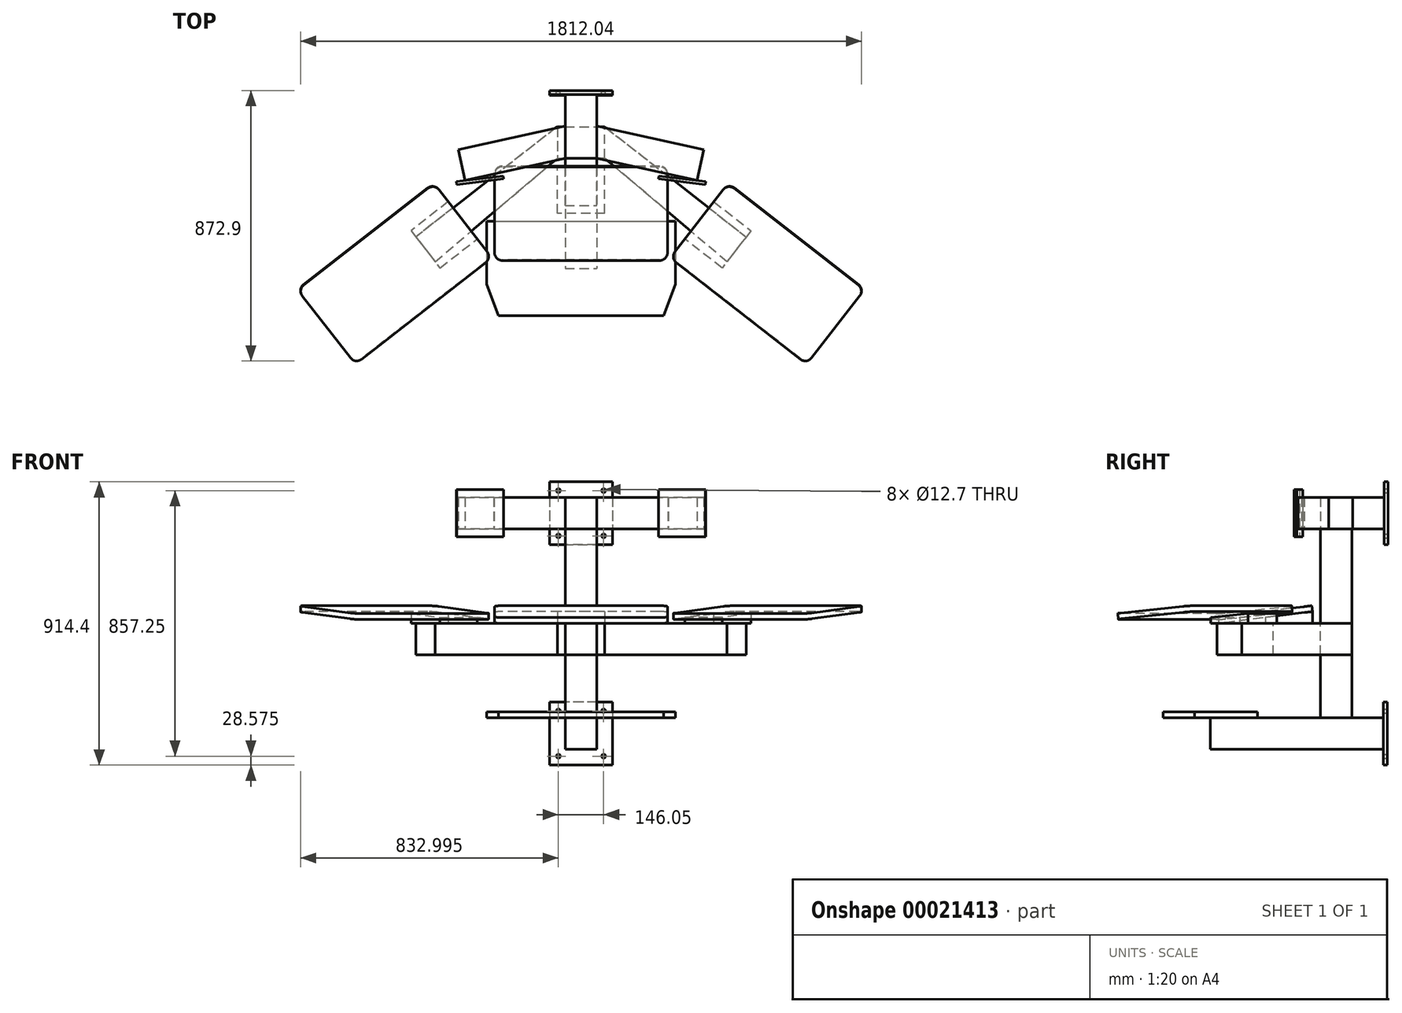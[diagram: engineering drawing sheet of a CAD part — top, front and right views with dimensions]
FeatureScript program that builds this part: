
annotation { "Feature Type Name" : "Feature", "Feature Type Description" : "" }
export const myFeature = defineFeature(function(context is Context, id is Id, definition is map)
    precondition{}
    {
        {
            var Q0;
            Q0=qCreatedBy(makeId("Top.planeOp"),FACE);
            var sketch = newSketch(context, id + "F0", { "sketchPlane" : qUnion([Q0])});
            skLineSegment(sketch, "E0", {"start": v(0, 189.9) * mm, "end": v(-50.8, 189.9) * mm});
            skLineSegment(sketch, "E1", {"start": v(-50.8, 189.9) * mm, "end": v(-50.8, 88.3) * mm});
            skLineSegment(sketch, "E2", {"start": v(-50.8, 88.3) * mm, "end": v(-396.31, 11.25) * mm});
            skLineSegment(sketch, "E3", {"start": v(-396.31, 11.25) * mm, "end": v(-374.2, -87.91) * mm});
            skLineSegment(sketch, "E4", {"start": v(-374.2, -87.91) * mm, "end": v(-50.8, -15.8) * mm});
            skLineSegment(sketch, "E5", {"start": v(-50.8, -15.8) * mm, "end": v(0, -15.8) * mm});
            skLineSegment(sketch, "E6", {"start": v(0, -15.8) * mm, "end": v(0, 189.9) * mm});
            skLineSegment(sketch, "E7.MirrorCS", {"start": v(0, 189.9) * mm, "end": v(50.8, 189.9) * mm});
            skLineSegment(sketch, "E8.MirrorCS", {"start": v(50.8, 189.9) * mm, "end": v(50.8, 88.3) * mm});
            skLineSegment(sketch, "E9.MirrorCS", {"start": v(50.8, 88.3) * mm, "end": v(396.31, 11.25) * mm});
            skLineSegment(sketch, "E10.MirrorCS", {"start": v(396.31, 11.25) * mm, "end": v(374.2, -87.91) * mm});
            skLineSegment(sketch, "E11.MirrorCS", {"start": v(374.2, -87.91) * mm, "end": v(50.8, -15.8) * mm});
            skLineSegment(sketch, "E12.MirrorCS", {"start": v(50.8, -15.8) * mm, "end": v(0, -15.8) * mm});
            skLineSegment(sketch, "E13", {"start": v(-50.8, 88.3) * mm, "end": v(-50.8, -15.8) * mm});
            skLineSegment(sketch, "E14", {"start": v(50.8, 88.3) * mm, "end": v(50.8, -15.8) * mm});
            skLineSegment(sketch, "E15", {"start": v(-50.8, 189.9) * mm, "end": v(-101.6, 189.9) * mm});
            skLineSegment(sketch, "E16", {"start": v(-101.6, 189.9) * mm, "end": v(-101.6, 202.6) * mm});
            skLineSegment(sketch, "E17", {"start": v(-101.6, 202.6) * mm, "end": v(0, 202.6) * mm});
            skLineSegment(sketch, "E18", {"start": v(0, 202.6) * mm, "end": v(0, 189.9) * mm});
            skLineSegment(sketch, "E19.MirrorCS", {"start": v(101.6, 202.6) * mm, "end": v(0, 202.6) * mm});
            skLineSegment(sketch, "E20.MirrorCS", {"start": v(101.6, 189.9) * mm, "end": v(101.6, 202.6) * mm});
            skLineSegment(sketch, "E21.MirrorCS", {"start": v(50.8, 189.9) * mm, "end": v(101.6, 189.9) * mm});
            skLineSegment(sketch, "E22", {"start": v(-374.2, -87.91) * mm, "end": v(-280.2, -76.7) * mm});
            skLineSegment(sketch, "E23", {"start": v(-280.2, -76.7) * mm, "end": v(-282.27, -67.41) * mm});
            skLineSegment(sketch, "E24", {"start": v(-280.2, -76.7) * mm, "end": v(-251.54, -73.3) * mm});
            skLineSegment(sketch, "E25", {"start": v(-251.54, -73.3) * mm, "end": v(-250.4, -82.75) * mm});
            skLineSegment(sketch, "E26", {"start": v(-250.4, -82.75) * mm, "end": v(-401.74, -100.78) * mm});
            skLineSegment(sketch, "E27", {"start": v(-401.74, -100.78) * mm, "end": v(-402.86, -91.33) * mm});
            skLineSegment(sketch, "E28", {"start": v(-402.86, -91.33) * mm, "end": v(-374.2, -87.91) * mm});
            skLineSegment(sketch, "E29.MirrorCS", {"start": v(280.2, -76.7) * mm, "end": v(282.27, -67.41) * mm});
            skLineSegment(sketch, "E30.MirrorCS", {"start": v(251.54, -73.3) * mm, "end": v(250.4, -82.75) * mm});
            skLineSegment(sketch, "E31.MirrorCS", {"start": v(280.2, -76.7) * mm, "end": v(251.54, -73.3) * mm});
            skLineSegment(sketch, "E32.MirrorCS", {"start": v(374.2, -87.91) * mm, "end": v(280.2, -76.7) * mm});
            skLineSegment(sketch, "E33.MirrorCS", {"start": v(402.86, -91.33) * mm, "end": v(374.2, -87.91) * mm});
            skLineSegment(sketch, "E34.MirrorCS", {"start": v(401.74, -100.78) * mm, "end": v(402.86, -91.33) * mm});
            skLineSegment(sketch, "E35.MirrorCS", {"start": v(250.4, -82.75) * mm, "end": v(401.74, -100.78) * mm});
            skLineSegment(sketch, "E36", {"start": v(50.8, 88.3) * mm, "end": v(-50.8, 88.3) * mm});
            skPoint(sketch, "E37", {"position": v(0, 88.3) * mm});
            skPoint(sketch, "E38", {"position": v(-326.07, -91.77) * mm});
            skPoint(sketch, "E39", {"position": v(326.07, -91.77) * mm});
            skSolve(sketch);
        }
        {
            var Q0;
            Q0=makeQuery(id+"F0.imprint","IMPRINT",FACE,{"disambiguationData":[TD([[makeQuery(id+"F0.imprint","IMPRINT",EDGE,{"derivedFrom":sQuery(id+"F0.wireOp",EDGE,"E0")}),1.0]])]});
            var Q1;
            Q1=makeQuery(id+"F0.imprint","IMPRINT",FACE,{"disambiguationData":[TD([[makeQuery(id+"F0.imprint","IMPRINT",EDGE,{"derivedFrom":sQuery(id+"F0.wireOp",EDGE,"E6")}),-1.0]])]});
            var Q2;
            {var subQ4=sQuery(id+"F0.wireOp",EDGE,"E5");Q2=makeQuery(id+"F0.imprint","IMPRINT",FACE,{"disambiguationData":[TD([[makeQuery(id+"F0.imprint","IMPRINT",EDGE,{"derivedFrom":subQ4}),1.0]])]});}
            extrude(context, id + "F1", {"entities" : qUnion([Q0, Q1, Q2]), "depth" : 101.6 * mm, "symmetric" : true});
        }
        {
            var Q0;
            Q0=makeQuery(id+"F0.imprint","IMPRINT",FACE,{"disambiguationData":[TD([[makeQuery(id+"F0.imprint","IMPRINT",EDGE,{"derivedFrom":sQuery(id+"F0.wireOp",EDGE,"E0")}),-1.0]])]});
            var Q1;
            Q1=makeQuery(id+"F0.imprint","IMPRINT",FACE,{"disambiguationData":[TD([[makeQuery(id+"F0.imprint","IMPRINT",EDGE,{"derivedFrom":sQuery(id+"F0.wireOp",EDGE,"E18")}),1.0]])]});
            extrude(context, id + "F2", {"entities" : qUnion([Q0, Q1]), "depth" : 203.2 * mm, "symmetric" : true});
        }
        {
            var Q0;
            Q0=makeQuery(id+"F0.imprint","IMPRINT",FACE,{"disambiguationData":[TD([[makeQuery(id+"F0.imprint","IMPRINT",EDGE,{"derivedFrom":sQuery(id+"F0.wireOp",EDGE,"E2")}),1.0]])]});
            extrude(context, id + "F3", {"entities" : qUnion([Q0]), "depth" : 101.6 * mm, "symmetric" : true});
        }
        {
            var Q0;
            Q0=makeQuery(id+"F0.imprint","IMPRINT",FACE,{"disambiguationData":[TD([[makeQuery(id+"F0.imprint","IMPRINT",EDGE,{"derivedFrom":sQuery(id+"F0.wireOp",EDGE,"E9.MirrorCS")}),-1.0]])]});
            extrude(context, id + "F4", {"entities" : qUnion([Q0]), "depth" : 101.6 * mm, "symmetric" : true});
        }
        {
            var Q0;
            {var subQ1=sQuery(id+"F0.wireOp",EDGE,"E22");Q0=makeQuery(id+"F0.imprint","IMPRINT",FACE,{"disambiguationData":[TD([[makeQuery(id+"F0.imprint","IMPRINT",EDGE,{"derivedFrom":subQ1}),1.0]])]});}
            extrude(context, id + "F5", {"entities" : qUnion([Q0]), "depth" : 101.6 * mm, "symmetric" : true});
        }
        {
            var Q0;
            {var subQ0=sQuery(id+"F0.wireOp",EDGE,"E29.MirrorCS");Q0=makeQuery(id+"F0.imprint","IMPRINT",FACE,{"disambiguationData":[TD([[makeQuery(id+"F0.imprint","IMPRINT",EDGE,{"derivedFrom":subQ0}),-1.0]])]});}
            extrude(context, id + "F6", {"entities" : qUnion([Q0]), "depth" : 101.6 * mm, "symmetric" : true});
        }
        {
            var Q0;
            Q0=makeQuery(id+"F0.imprint","IMPRINT",FACE,{"disambiguationData":[TD([[makeQuery(id+"F0.imprint","IMPRINT",EDGE,{"derivedFrom":sQuery(id+"F0.wireOp",EDGE,"E22")}),-1.0]])]});
            var Q1;
            Q1=makeQuery(id+"F0.imprint","IMPRINT",FACE,{"disambiguationData":[TD([[makeQuery(id+"F0.imprint","IMPRINT",EDGE,{"derivedFrom":sQuery(id+"F0.wireOp",EDGE,"E30.MirrorCS")}),1.0]])]});
            extrude(context, id + "F7", {"entities" : qUnion([Q0, Q1]), "depth" : 152.4 * mm, "symmetric" : true});
        }
        {
            var Q0;
            Q0=makeQuery(id+"F2.opExtrude","SWEPT_FACE",FACE,{"disambiguationData":[OSD([sQuery(id+"F0.wireOp",EDGE,"E0"),sQuery(id+"F0.wireOp",EDGE,"E15"),sQuery(id+"F0.wireOp",EDGE,"E21.MirrorCS"),sQuery(id+"F0.wireOp",EDGE,"E7.MirrorCS")])]});
            var sketch = newSketch(context, id + "F8", { "sketchPlane" : qUnion([Q0])});
            skLineSegment(sketch, "E40", {"start": v(-73.02, 101.6) * mm, "end": v(-73.02, -101.6) * mm, "construction": true});
            skLineSegment(sketch, "E41", {"start": v(73.03, -101.6) * mm, "end": v(73.03, 101.6) * mm, "construction": true});
            skLineSegment(sketch, "E42", {"start": v(101.6, 73.02) * mm, "end": v(-101.6, 73.02) * mm, "construction": true});
            skLineSegment(sketch, "E43", {"start": v(-101.6, -73.03) * mm, "end": v(101.6, -73.03) * mm, "construction": true});
            skPoint(sketch, "E44", {"position": v(-73.02, 73.02) * mm});
            skPoint(sketch, "E45", {"position": v(73.03, 73.02) * mm});
            skPoint(sketch, "E46", {"position": v(73.03, -73.03) * mm});
            skPoint(sketch, "E47", {"position": v(-73.02, -73.03) * mm});
            skSolve(sketch);
        }
        {
            var Q0;
            Q0=makeQuery(id+"F1.opExtrude","CAP_FACE",FACE,{"disambiguationData":[OSD([sQuery(id+"F0.wireOp",EDGE,"E0"),sQuery(id+"F0.wireOp",EDGE,"E1"),sQuery(id+"F0.wireOp",EDGE,"E5"),sQuery(id+"F0.wireOp",EDGE,"E8.MirrorCS"),sQuery(id+"F0.wireOp",EDGE,"E12.MirrorCS"),sQuery(id+"F0.wireOp",EDGE,"E13"),sQuery(id+"F0.wireOp",EDGE,"E14"),sQuery(id+"F0.wireOp",EDGE,"E7.MirrorCS")])],"isStart":true});
            var sketch = newSketch(context, id + "F9", { "sketchPlane" : qUnion([Q0])});
            skLineSegment(sketch, "E48.bottom", {"start": v(-50.8, 15.8) * mm, "end": v(50.8, 15.8) * mm});
            skLineSegment(sketch, "E48.top", {"start": v(-50.8, -85.8) * mm, "end": v(50.8, -85.8) * mm});
            skLineSegment(sketch, "E48.left", {"start": v(-50.8, 15.8) * mm, "end": v(-50.8, -85.8) * mm});
            skLineSegment(sketch, "E48.right", {"start": v(50.8, 15.8) * mm, "end": v(50.8, -85.8) * mm});
            skSolve(sketch);
        }
        {
            var Q0;
            Q0=makeQuery(id+"F9.imprint","IMPRINT",FACE,{"disambiguationData":[TD([[makeQuery(id+"F9.imprint","IMPRINT",EDGE,{"derivedFrom":sQuery(id+"F9.wireOp",EDGE,"E48.bottom")}),1.0]])]});
            extrude(context, id + "F10", {"entities" : qUnion([Q0]), "depth" : 609.6 * mm});
        }
        {
            var Q0;
            Q0=makeQuery(id+"F10.opExtrude","CAP_FACE",FACE,{"disambiguationData":[OSD([sQuery(id+"F9.wireOp",EDGE,"E48.bottom"),sQuery(id+"F9.wireOp",EDGE,"E48.top"),sQuery(id+"F9.wireOp",EDGE,"E48.left"),sQuery(id+"F9.wireOp",EDGE,"E48.right")])],"isStart":false});
            var sketch = newSketch(context, id + "F11", { "sketchPlane" : qUnion([Q0])});
            skLineSegment(sketch, "E49", {"start": v(-50.8, 15.8) * mm, "end": v(-50.8, 371.4) * mm});
            skLineSegment(sketch, "E50", {"start": v(-50.8, 371.4) * mm, "end": v(0, 371.4) * mm});
            skLineSegment(sketch, "E51", {"start": v(0, 371.4) * mm, "end": v(0, -187.4) * mm});
            skLineSegment(sketch, "E52", {"start": v(0, -187.4) * mm, "end": v(-50.8, -187.4) * mm});
            skLineSegment(sketch, "E53", {"start": v(-50.8, -187.4) * mm, "end": v(-50.8, 15.8) * mm});
            skLineSegment(sketch, "E54.MirrorCS", {"start": v(50.8, 371.4) * mm, "end": v(0, 371.4) * mm});
            skLineSegment(sketch, "E55.MirrorCS", {"start": v(50.8, 15.8) * mm, "end": v(50.8, 371.4) * mm});
            skLineSegment(sketch, "E56.MirrorCS", {"start": v(50.8, -187.4) * mm, "end": v(50.8, 15.8) * mm});
            skLineSegment(sketch, "E57.MirrorCS", {"start": v(0, -187.4) * mm, "end": v(50.8, -187.4) * mm});
            skLineSegment(sketch, "E58.MirrorCS", {"start": v(-50.8, 15.8) * mm, "end": v(50.8, 15.8) * mm});
            skLineSegment(sketch, "E59", {"start": v(0, -209.13) * mm, "end": v(0, -187.4) * mm});
            skSolve(sketch);
        }
        {
            var Q0;
            {var subQ3=sQuery(id+"F11.wireOp",EDGE,"E49");Q0=makeQuery(id+"F11.imprint","IMPRINT",FACE,{"disambiguationData":[TD([[makeQuery(id+"F11.imprint","IMPRINT",EDGE,{"derivedFrom":subQ3}),-1.0]])]});}
            var Q1;
            {var subQ4=sQuery(id+"F11.wireOp",EDGE,"E54.MirrorCS");Q1=makeQuery(id+"F11.imprint","IMPRINT",FACE,{"disambiguationData":[TD([[makeQuery(id+"F11.imprint","IMPRINT",EDGE,{"derivedFrom":subQ4}),1.0]])]});}
            var Q2;
            {var subQ1=sQuery(id+"F11.wireOp",EDGE,"E51");var subQ5=sQuery(id+"F11.wireOp",EDGE,"E58.MirrorCS");var subQ6=makeQuery(id+"F11.imprint","INTERSECT",VERTEX,{"derivedFrom":[subQ1,subQ5]});Q2=makeQuery(id+"F11.imprint","IMPRINT",FACE,{"disambiguationData":[TD([[makeQuery(id+"F11.imprint","IMPRINT",EDGE,{"disambiguationData":[TD([[subQ6,-1.0]])],"derivedFrom":subQ1}),1.0]])]});}
            var Q3;
            {var subQ1=sQuery(id+"F11.wireOp",EDGE,"E51");var subQ5=sQuery(id+"F11.wireOp",EDGE,"E58.MirrorCS");var subQ6=makeQuery(id+"F11.imprint","INTERSECT",VERTEX,{"derivedFrom":[subQ1,subQ5]});Q3=makeQuery(id+"F11.imprint","IMPRINT",FACE,{"disambiguationData":[TD([[makeQuery(id+"F11.imprint","IMPRINT",EDGE,{"disambiguationData":[TD([[subQ6,-1.0]])],"derivedFrom":subQ1}),-1.0]])]});}
            var Q4;
            {var subQ5=sQuery(id+"F11.wireOp",EDGE,"E52");Q4=makeQuery(id+"F11.imprint","IMPRINT",FACE,{"disambiguationData":[TD([[makeQuery(id+"F11.imprint","IMPRINT",EDGE,{"derivedFrom":subQ5}),-1.0]])]});}
            var Q5;
            {var subQ5=sQuery(id+"F11.wireOp",EDGE,"E57.MirrorCS");Q5=makeQuery(id+"F11.imprint","IMPRINT",FACE,{"disambiguationData":[TD([[makeQuery(id+"F11.imprint","IMPRINT",EDGE,{"derivedFrom":subQ5}),1.0]])]});}
            extrude(context, id + "F12", {"entities" : qUnion([Q0, Q1, Q2, Q3, Q4, Q5]), "depth" : 101.6 * mm});
        }
        {
            var Q0;
            Q0=makeQuery(id+"F12.opExtrude","SWEPT_FACE",FACE,{"disambiguationData":[OSD([sQuery(id+"F11.wireOp",EDGE,"E57.MirrorCS"),sQuery(id+"F11.wireOp",EDGE,"E52")])]});
            var sketch = newSketch(context, id + "F13", { "sketchPlane" : qUnion([Q0])});
            skLineSegment(sketch, "E60.rect.bottom", {"start": v(-101.6, -609.6) * mm, "end": v(101.6, -609.6) * mm});
            skLineSegment(sketch, "E60.rect.top", {"start": v(-101.6, -812.8) * mm, "end": v(101.6, -812.8) * mm});
            skLineSegment(sketch, "E60.rect.left", {"start": v(-101.6, -609.6) * mm, "end": v(-101.6, -812.8) * mm});
            skLineSegment(sketch, "E60.rect.right", {"start": v(101.6, -609.6) * mm, "end": v(101.6, -812.8) * mm});
            skPoint(sketch, "E60.rect.middle", {"position": v(0, -711.2) * mm});
            skLineSegment(sketch, "E61", {"start": v(-50.8, -711.2) * mm, "end": v(50.8, -711.2) * mm, "construction": true});
            skLineSegment(sketch, "E62", {"start": v(0, -660.4) * mm, "end": v(0, -762) * mm, "construction": true});
            skLineSegment(sketch, "E63", {"start": v(-101.6, -638.18) * mm, "end": v(101.6, -638.18) * mm, "construction": true});
            skLineSegment(sketch, "E64", {"start": v(101.6, -784.23) * mm, "end": v(-101.6, -784.23) * mm, "construction": true});
            skLineSegment(sketch, "E65", {"start": v(-73.03, -609.6) * mm, "end": v(-73.03, -812.8) * mm, "construction": true});
            skLineSegment(sketch, "E66", {"start": v(73.02, -812.8) * mm, "end": v(73.02, -609.6) * mm, "construction": true});
            skPoint(sketch, "E67", {"position": v(-73.03, -638.18) * mm});
            skPoint(sketch, "E68", {"position": v(73.02, -638.18) * mm});
            skPoint(sketch, "E69", {"position": v(73.02, -784.23) * mm});
            skPoint(sketch, "E70", {"position": v(-73.03, -784.23) * mm});
            skSolve(sketch);
        }
        {
            var Q0;
            Q0=makeQuery(id+"F13.imprint","IMPRINT",FACE,{"disambiguationData":[TD([[makeQuery(id+"F13.imprint","IMPRINT",EDGE,{"derivedFrom":sQuery(id+"F13.wireOp",EDGE,"E60.rect.bottom")}),-1.0]])]});
            var Q1;
            {var subQ1=sQuery(id+"F11.wireOp",EDGE,"E52");Q1=makeQuery(id+"F13.imprint","IMPRINT",FACE,{"disambiguationData":[TD([[makeQuery(id+"F13.imprint","IMPRINT",EDGE,{"derivedFrom":makeQuery(id+"F12.opExtrude","SWEPT_EDGE",EDGE,{"disambiguationData":[OSD([sQuery(id+"F11.wireOp",EDGE,"E53"),subQ1])]})}),1.0]])]});}
            extrude(context, id + "F14", {"entities" : qUnion([Q0, Q1]), "depth" : 12.7 * mm});
        }
        {
            var Q0;
            Q0=sQuery(id+"F8.wireOp",VERTEX,"E44");
            var Q1;
            Q1=sQuery(id+"F8.wireOp",VERTEX,"E45");
            var Q2;
            Q2=sQuery(id+"F8.wireOp",VERTEX,"E46");
            var Q3;
            Q3=sQuery(id+"F8.wireOp",VERTEX,"E47");
            var Q4;
            Q4=sQuery(id+"F13.wireOp",VERTEX,"E67");
            var Q5;
            Q5=sQuery(id+"F13.wireOp",VERTEX,"E68");
            var Q6;
            Q6=sQuery(id+"F13.wireOp",VERTEX,"E69");
            var Q7;
            Q7=sQuery(id+"F13.wireOp",VERTEX,"E70");
            var Q8;
            Q8=makeQuery(id+"F2.opExtrude","SWEPT_BODY",BODY,{"disambiguationData":[OSD([sQuery(id+"F0.wireOp",EDGE,"E0"),sQuery(id+"F0.wireOp",EDGE,"E15"),sQuery(id+"F0.wireOp",EDGE,"E16"),sQuery(id+"F0.wireOp",EDGE,"E17"),sQuery(id+"F0.wireOp",EDGE,"E19.MirrorCS"),sQuery(id+"F0.wireOp",EDGE,"E20.MirrorCS"),sQuery(id+"F0.wireOp",EDGE,"E21.MirrorCS"),sQuery(id+"F0.wireOp",EDGE,"E7.MirrorCS")])]});
            hole(context, id + "F15", {"style" : HoleStyle.SIMPLE, "holeDiameter" : 12.7 * mm, "endStyle" : HoleEndStyle.THROUGH, "locations" : qUnion([Q0, Q1, Q2, Q3, Q4, Q5, Q6, Q7]), "scope" : qUnion([Q8])});
        }
        {
            var Q0;
            Q0=sQuery(id+"F13.wireOp",VERTEX,"E67");
            var Q1;
            Q1=sQuery(id+"F13.wireOp",VERTEX,"E68");
            var Q2;
            Q2=sQuery(id+"F13.wireOp",VERTEX,"E69");
            var Q3;
            Q3=sQuery(id+"F13.wireOp",VERTEX,"E70");
            var Q4;
            Q4=makeQuery(id+"F14.opExtrude","SWEPT_BODY",BODY,{"disambiguationData":[OSD([sQuery(id+"F13.wireOp",EDGE,"E60.rect.bottom"),sQuery(id+"F13.wireOp",EDGE,"E60.rect.top"),sQuery(id+"F13.wireOp",EDGE,"E60.rect.left"),sQuery(id+"F13.wireOp",EDGE,"E60.rect.right")])]});
            hole(context, id + "F16", {"style" : HoleStyle.SIMPLE, "holeDiameter" : 12.7 * mm, "endStyle" : HoleEndStyle.THROUGH, "oppositeDirection" : true, "locations" : qUnion([Q0, Q1, Q2, Q3]), "scope" : qUnion([Q4])});
        }
        {
            var Q0;
            Q0=makeQuery(id+"F12.opExtrude","CAP_FACE",FACE,{"disambiguationData":[OSD([sQuery(id+"F11.wireOp",EDGE,"E49"),sQuery(id+"F11.wireOp",EDGE,"E50"),sQuery(id+"F11.wireOp",EDGE,"E53"),sQuery(id+"F11.wireOp",EDGE,"E54.MirrorCS"),sQuery(id+"F11.wireOp",EDGE,"E55.MirrorCS"),sQuery(id+"F11.wireOp",EDGE,"E56.MirrorCS"),sQuery(id+"F11.wireOp",EDGE,"E57.MirrorCS"),sQuery(id+"F11.wireOp",EDGE,"E52")])],"isStart":true});
            var sketch = newSketch(context, id + "F17", { "sketchPlane" : qUnion([Q0])});
            skLineSegment(sketch, "E71.rect.bottom", {"start": v(-304.8, -219) * mm, "end": v(304.8, -219) * mm});
            skLineSegment(sketch, "E71.rect.left", {"start": v(-304.8, -219) * mm, "end": v(-304.8, -422.2) * mm});
            skLineSegment(sketch, "E71.rect.right", {"start": v(304.8, -219) * mm, "end": v(304.8, -422.2) * mm});
            skPoint(sketch, "E71.rect.middle", {"position": v(0, -371.4) * mm});
            skLineSegment(sketch, "E72", {"start": v(-266.7, -523.8) * mm, "end": v(266.7, -523.8) * mm});
            skLineSegment(sketch, "E73", {"start": v(304.8, -422.2) * mm, "end": v(266.7, -523.8) * mm});
            skLineSegment(sketch, "E74", {"start": v(-304.8, -422.2) * mm, "end": v(-266.7, -523.8) * mm});
            skSolve(sketch);
        }
        {
            var Q0;
            Q0 = qSketchRegion(id + "F17", true);
            extrude(context, id + "F18", {"entities" : qUnion([Q0]), "depth" : 19.05 * mm});
        }
        {
            var Q0;
            Q0=makeQuery(id+"F10.opExtrude","SWEPT_FACE",FACE,{"disambiguationData":[OSD([sQuery(id+"F9.wireOp",EDGE,"E48.right")])]});
            var sketch = newSketch(context, id + "F19", { "sketchPlane" : qUnion([Q0])});
            skLineSegment(sketch, "E75.bottom", {"start": v(-15.8, -355.6) * mm, "end": v(85.8, -355.6) * mm});
            skLineSegment(sketch, "E75.top", {"start": v(-15.8, -457.2) * mm, "end": v(85.8, -457.2) * mm});
            skLineSegment(sketch, "E75.left", {"start": v(-15.8, -355.6) * mm, "end": v(-15.8, -457.2) * mm});
            skLineSegment(sketch, "E75.right", {"start": v(85.8, -355.6) * mm, "end": v(85.8, -457.2) * mm});
            skSolve(sketch);
        }
        {
            var Q0;
            Q0=makeQuery(id+"F19.imprint","IMPRINT",FACE,{"disambiguationData":[TD([[makeQuery(id+"F19.imprint","IMPRINT",EDGE,{"derivedFrom":sQuery(id+"F19.wireOp",EDGE,"E75.bottom")}),-1.0]])]});
            extrude(context, id + "F20", {"entities" : qUnion([Q0]), "depth" : 25.4 * mm});
        }
        {
            var Q0;
            Q0=makeQuery(id+"F10.opExtrude","SWEPT_FACE",FACE,{"disambiguationData":[OSD([sQuery(id+"F9.wireOp",EDGE,"E48.left")])]});
            var sketch = newSketch(context, id + "F21", { "sketchPlane" : qUnion([Q0])});
            skLineSegment(sketch, "E76.bottom", {"start": v(-85.8, -355.6) * mm, "end": v(15.8, -355.6) * mm});
            skLineSegment(sketch, "E76.top", {"start": v(-85.8, -457.2) * mm, "end": v(15.8, -457.2) * mm});
            skLineSegment(sketch, "E76.left", {"start": v(-85.8, -355.6) * mm, "end": v(-85.8, -457.2) * mm});
            skLineSegment(sketch, "E76.right", {"start": v(15.8, -355.6) * mm, "end": v(15.8, -457.2) * mm});
            skSolve(sketch);
        }
        {
            var Q0;
            Q0 = qSketchRegion(id + "F21", true);
            extrude(context, id + "F22", {"entities" : qUnion([Q0]), "depth" : 25.4 * mm});
        }
        {
            var Q0;
            Q0=makeQuery(id+"F20.opExtrude","SWEPT_FACE",FACE,{"disambiguationData":[OSD([sQuery(id+"F19.wireOp",EDGE,"E75.bottom")])]});
            var sketch = newSketch(context, id + "F23", { "sketchPlane" : qUnion([Q0])});
            skLineSegment(sketch, "E77", {"start": v(76.2, 85.8) * mm, "end": v(-941.99, 85.8) * mm, "construction": true});
            skLineSegment(sketch, "E78", {"start": v(76.2, 85.8) * mm, "end": v(1576.96, 85.8) * mm, "construction": true});
            skLineSegment(sketch, "E79", {"start": v(0, 85.8) * mm, "end": v(0, -1109.54) * mm, "construction": true});
            skLineSegment(sketch, "E80", {"start": v(-946.7, -244.4) * mm, "end": v(1642.87, -244.4) * mm, "construction": true});
            skLineSegment(sketch, "E81", {"start": v(76.2, 85.8) * mm, "end": v(533.4, -269.8) * mm});
            skLineSegment(sketch, "E82", {"start": v(533.4, -269.8) * mm, "end": v(471.02, -350) * mm});
            skLineSegment(sketch, "E83", {"start": v(471.02, -350) * mm, "end": v(76.2, -15.8) * mm});
            skLineSegment(sketch, "E84.MirrorCS", {"start": v(-76.2, 85.8) * mm, "end": v(-533.4, -269.8) * mm});
            skLineSegment(sketch, "E85.MirrorCS", {"start": v(-533.4, -269.8) * mm, "end": v(-471.02, -350) * mm});
            skLineSegment(sketch, "E86.MirrorCS", {"start": v(-471.02, -350) * mm, "end": v(-76.2, -15.8) * mm});
            skLineSegment(sketch, "E87", {"start": v(76.2, 85.8) * mm, "end": v(76.2, -15.8) * mm});
            skLineSegment(sketch, "E88.MirrorCS", {"start": v(-76.2, 85.8) * mm, "end": v(-76.2, -15.8) * mm});
            skSolve(sketch);
        }
        {
            var Q0;
            Q0=makeQuery(id+"F23.imprint","IMPRINT",FACE,{"disambiguationData":[TD([[makeQuery(id+"F23.imprint","IMPRINT",EDGE,{"derivedFrom":sQuery(id+"F23.wireOp",EDGE,"E81")}),-1.0]])]});
            var Q1;
            Q1=makeQuery(id+"F23.imprint","IMPRINT",FACE,{"disambiguationData":[TD([[makeQuery(id+"F23.imprint","IMPRINT",EDGE,{"derivedFrom":sQuery(id+"F23.wireOp",EDGE,"E84.MirrorCS")}),1.0]])]});
            extrude(context, id + "F24", {"entities" : qUnion([Q0, Q1]), "oppositeDirection" : true, "depth" : 101.6 * mm});
        }
        {
            var Q0;
            Q0=makeQuery(id+"F10.opExtrude","SWEPT_FACE",FACE,{"disambiguationData":[OSD([sQuery(id+"F9.wireOp",EDGE,"E48.bottom")])]});
            var sketch = newSketch(context, id + "F25", { "sketchPlane" : qUnion([Q0])});
            skLineSegment(sketch, "E89.bottom", {"start": v(-50.8, -355.6) * mm, "end": v(50.8, -355.6) * mm});
            skLineSegment(sketch, "E89.top", {"start": v(-50.8, -456.5) * mm, "end": v(50.8, -456.5) * mm});
            skLineSegment(sketch, "E89.left", {"start": v(-50.8, -355.6) * mm, "end": v(-50.8, -456.5) * mm});
            skLineSegment(sketch, "E89.right", {"start": v(50.8, -355.6) * mm, "end": v(50.8, -456.5) * mm});
            skSolve(sketch);
        }
        {
            var Q0;
            Q0=makeQuery(id+"F25.imprint","IMPRINT",FACE,{"disambiguationData":[TD([[makeQuery(id+"F25.imprint","IMPRINT",EDGE,{"derivedFrom":sQuery(id+"F25.wireOp",EDGE,"E89.bottom")}),-1.0]])]});
            extrude(context, id + "F26", {"entities" : qUnion([Q0]), "depth" : 152.4 * mm});
        }
        {
            var Q0;
            Q0=makeQuery(id+"F24.opExtrude","CAP_FACE",FACE,{"disambiguationData":[OSD([sQuery(id+"F23.wireOp",EDGE,"E84.MirrorCS"),sQuery(id+"F23.wireOp",EDGE,"E85.MirrorCS"),sQuery(id+"F23.wireOp",EDGE,"E86.MirrorCS"),sQuery(id+"F23.wireOp",EDGE,"E88.MirrorCS")])],"isStart":true});
            var sketch = newSketch(context, id + "F27", { "sketchPlane" : qUnion([Q0])});
            skLineSegment(sketch, "E90", {"start": v(-428.7, -156.18) * mm, "end": v(-549, -249.74) * mm});
            skLineSegment(sketch, "E91", {"start": v(-549, -249.74) * mm, "end": v(-455.43, -370.04) * mm});
            skLineSegment(sketch, "E92", {"start": v(-455.43, -370.04) * mm, "end": v(-335.13, -276.48) * mm});
            skLineSegment(sketch, "E93", {"start": v(-502.21, -309.9) * mm, "end": v(-417.72, -244.17) * mm, "construction": true});
            skLineSegment(sketch, "E94", {"start": v(-335.13, -276.48) * mm, "end": v(-428.7, -156.18) * mm});
            skLineSegment(sketch, "E95", {"start": v(-488.85, -202.96) * mm, "end": v(-442.06, -263.11) * mm, "construction": true});
            skLineSegment(sketch, "E96", {"start": v(-381.91, -216.33) * mm, "end": v(-442.06, -263.11) * mm, "construction": true});
            skLineSegment(sketch, "E97", {"start": v(-442.06, -263.11) * mm, "end": v(-395.28, -323.26) * mm, "construction": true});
            skLineSegment(sketch, "E98", {"start": v(-442.06, -263.11) * mm, "end": v(-502.21, -309.9) * mm, "construction": true});
            skLineSegment(sketch, "E99", {"start": v(-417.72, -244.17) * mm, "end": v(-103.61, 0.13) * mm, "construction": true});
            skSolve(sketch);
        }
        {
            var Q0;
            {var subQ5=sQuery(id+"F27.wireOp",EDGE,"E90");Q0=makeQuery(id+"F27.imprint","IMPRINT",FACE,{"disambiguationData":[TD([[makeQuery(id+"F27.imprint","IMPRINT",EDGE,{"derivedFrom":subQ5}),1.0]])]});}
            var Q1;
            {var subQ3=sQuery(id+"F27.wireOp",EDGE,"E91");var subQ5=makeQuery(id+"F24.opExtrude","CAP_EDGE",EDGE,{"disambiguationData":[OSD([sQuery(id+"F23.wireOp",EDGE,"E84.MirrorCS")])],"isStart":true});var subQ7=makeQuery(id+"F27.imprint","INTERSECT",VERTEX,{"derivedFrom":[subQ5,subQ3]});Q1=makeQuery(id+"F27.imprint","IMPRINT",FACE,{"disambiguationData":[TD([[makeQuery(id+"F27.imprint","IMPRINT",EDGE,{"disambiguationData":[TD([[subQ7,-1.0]])],"derivedFrom":subQ3}),1.0]])]});}
            var Q2;
            {var subQ5=sQuery(id+"F27.wireOp",EDGE,"E92");Q2=makeQuery(id+"F27.imprint","IMPRINT",FACE,{"disambiguationData":[TD([[makeQuery(id+"F27.imprint","IMPRINT",EDGE,{"derivedFrom":subQ5}),1.0]])]});}
            extrude(context, id + "F28", {"entities" : qUnion([Q0, Q1, Q2]), "depth" : 19.05 * mm});
        }
        {
            var Q0;
            Q0=makeQuery(id+"F24.opExtrude","CAP_FACE",FACE,{"disambiguationData":[OSD([sQuery(id+"F23.wireOp",EDGE,"E81"),sQuery(id+"F23.wireOp",EDGE,"E82"),sQuery(id+"F23.wireOp",EDGE,"E83"),sQuery(id+"F23.wireOp",EDGE,"E87")])],"isStart":true});
            var sketch = newSketch(context, id + "F29", { "sketchPlane" : qUnion([Q0])});
            skLineSegment(sketch, "E100", {"start": v(502.21, -309.9) * mm, "end": v(105.37, -1.24) * mm, "construction": true});
            skLineSegment(sketch, "E101", {"start": v(428.7, -156.18) * mm, "end": v(549, -249.74) * mm});
            skLineSegment(sketch, "E102", {"start": v(549, -249.74) * mm, "end": v(455.43, -370.04) * mm});
            skLineSegment(sketch, "E103", {"start": v(455.43, -370.04) * mm, "end": v(335.13, -276.48) * mm});
            skLineSegment(sketch, "E104", {"start": v(335.13, -276.48) * mm, "end": v(428.7, -156.18) * mm});
            skLineSegment(sketch, "E105", {"start": v(488.85, -202.96) * mm, "end": v(395.28, -323.26) * mm, "construction": true});
            skLineSegment(sketch, "E106", {"start": v(381.91, -216.33) * mm, "end": v(502.21, -309.9) * mm, "construction": true});
            skSolve(sketch);
        }
        {
            var Q0;
            {var subQ5=sQuery(id+"F29.wireOp",EDGE,"E101");Q0=makeQuery(id+"F29.imprint","IMPRINT",FACE,{"disambiguationData":[TD([[makeQuery(id+"F29.imprint","IMPRINT",EDGE,{"derivedFrom":subQ5}),-1.0]])]});}
            var Q1;
            {var subQ3=sQuery(id+"F29.wireOp",EDGE,"E102");var subQ5=makeQuery(id+"F24.opExtrude","CAP_EDGE",EDGE,{"disambiguationData":[OSD([sQuery(id+"F23.wireOp",EDGE,"E81")])],"isStart":true});var subQ7=makeQuery(id+"F29.imprint","INTERSECT",VERTEX,{"derivedFrom":[subQ5,subQ3]});Q1=makeQuery(id+"F29.imprint","IMPRINT",FACE,{"disambiguationData":[TD([[makeQuery(id+"F29.imprint","IMPRINT",EDGE,{"disambiguationData":[TD([[subQ7,-1.0]])],"derivedFrom":subQ3}),-1.0]])]});}
            var Q2;
            {var subQ5=sQuery(id+"F29.wireOp",EDGE,"E103");Q2=makeQuery(id+"F29.imprint","IMPRINT",FACE,{"disambiguationData":[TD([[makeQuery(id+"F29.imprint","IMPRINT",EDGE,{"derivedFrom":subQ5}),-1.0]])]});}
            extrude(context, id + "F30", {"entities" : qUnion([Q0, Q1, Q2]), "depth" : 19.05 * mm});
        }
        {
            var Q0;
            Q0=makeQuery(id+"F30.opExtrude","SWEPT_FACE",FACE,{"disambiguationData":[OSD([sQuery(id+"F29.wireOp",EDGE,"E102")])]});
            var sketch = newSketch(context, id + "F31", { "sketchPlane" : qUnion([Q0])});
            skLineSegment(sketch, "E107", {"start": v(139.91, -336.55) * mm, "end": v(139.91, -323.85) * mm});
            skLineSegment(sketch, "E108", {"start": v(139.91, -323.85) * mm, "end": v(-12.49, -336.55) * mm});
            skLineSegment(sketch, "E109", {"start": v(-12.49, -336.55) * mm, "end": v(139.91, -336.55) * mm});
            skSolve(sketch);
        }
        {
            var Q0;
            Q0=makeQuery(id+"F31.imprint","IMPRINT",FACE,{"disambiguationData":[TD([[makeQuery(id+"F31.imprint","IMPRINT",EDGE,{"derivedFrom":sQuery(id+"F31.wireOp",EDGE,"E107")}),1.0]])]});
            extrude(context, id + "F32", {"entities" : qUnion([Q0]), "operationType" : NewBodyOperationType.ADD, "oppositeDirection" : true, "depth" : 152.4 * mm});
        }
        {
            var Q0;
            Q0=makeQuery(id+"F28.opExtrude","SWEPT_FACE",FACE,{"disambiguationData":[OSD([sQuery(id+"F27.wireOp",EDGE,"E91")])]});
            var sketch = newSketch(context, id + "F33", { "sketchPlane" : qUnion([Q0])});
            skLineSegment(sketch, "E110", {"start": v(-139.91, -336.55) * mm, "end": v(-139.91, -323.85) * mm});
            skLineSegment(sketch, "E111", {"start": v(-139.91, -323.85) * mm, "end": v(12.49, -336.55) * mm});
            skLineSegment(sketch, "E112", {"start": v(12.49, -336.55) * mm, "end": v(-139.91, -336.55) * mm});
            skSolve(sketch);
        }
        {
            var Q0;
            Q0=makeQuery(id+"F33.imprint","IMPRINT",FACE,{"disambiguationData":[TD([[makeQuery(id+"F33.imprint","IMPRINT",EDGE,{"derivedFrom":sQuery(id+"F33.wireOp",EDGE,"E110")}),-1.0]])]});
            extrude(context, id + "F34", {"entities" : qUnion([Q0]), "operationType" : NewBodyOperationType.ADD, "oppositeDirection" : true, "depth" : 152.4 * mm});
        }
        {
            var Q0;
            Q0=makeQuery(id+"F26.opExtrude","SWEPT_FACE",FACE,{"disambiguationData":[OSD([sQuery(id+"F25.wireOp",EDGE,"E89.bottom")])]});
            var sketch = newSketch(context, id + "F35", { "sketchPlane" : qUnion([Q0])});
            skLineSegment(sketch, "E113", {"start": v(-50.8, -117.4) * mm, "end": v(50.8, -117.4) * mm, "construction": true});
            skLineSegment(sketch, "E114", {"start": v(0, -168.2) * mm, "end": v(0, -15.8) * mm, "construction": true});
            skLineSegment(sketch, "E115.rect.bottom", {"start": v(76.2, -193.6) * mm, "end": v(-76.2, -193.6) * mm});
            skLineSegment(sketch, "E115.rect.top", {"start": v(76.2, -41.2) * mm, "end": v(-76.2, -41.2) * mm});
            skLineSegment(sketch, "E115.rect.left", {"start": v(76.2, -193.6) * mm, "end": v(76.2, -41.2) * mm});
            skLineSegment(sketch, "E115.rect.right", {"start": v(-76.2, -193.6) * mm, "end": v(-76.2, -41.2) * mm});
            skPoint(sketch, "E115.rect.middle", {"position": v(0, -117.4) * mm});
            skSolve(sketch);
        }
        {
            var Q0;
            Q0 = qSketchRegion(id + "F35", true);
            extrude(context, id + "F36", {"entities" : qUnion([Q0]), "depth" : 19.05 * mm});
        }
        {
            var Q0;
            Q0=makeQuery(id+"F36.opExtrude","SWEPT_FACE",FACE,{"disambiguationData":[OSD([sQuery(id+"F35.wireOp",EDGE,"E115.rect.right")])]});
            var sketch = newSketch(context, id + "F37", { "sketchPlane" : qUnion([Q0])});
            skLineSegment(sketch, "E116", {"start": v(41.2, -336.55) * mm, "end": v(41.2, -317.3) * mm});
            skLineSegment(sketch, "E117", {"start": v(41.2, -317.3) * mm, "end": v(193.6, -336.55) * mm});
            skLineSegment(sketch, "E118", {"start": v(193.6, -336.55) * mm, "end": v(41.2, -336.55) * mm});
            skSolve(sketch);
        }
        {
            var Q0;
            Q0=makeQuery(id+"F37.imprint","IMPRINT",FACE,{"disambiguationData":[TD([[makeQuery(id+"F37.imprint","IMPRINT",EDGE,{"derivedFrom":sQuery(id+"F37.wireOp",EDGE,"E116")}),-1.0]])]});
            extrude(context, id + "F38", {"entities" : qUnion([Q0]), "operationType" : NewBodyOperationType.ADD, "oppositeDirection" : true, "depth" : 152.4 * mm});
        }
        {
            var Q0;
            Q0=makeQuery(id+"F38.opExtrude","SWEPT_FACE",FACE,{"disambiguationData":[OSD([sQuery(id+"F37.wireOp",EDGE,"E117")])]});
            var sketch = newSketch(context, id + "F39", { "sketchPlane" : qUnion([Q0])});
            skLineSegment(sketch, "E119.rect.bottom", {"start": v(254, -80.64) * mm, "end": v(-254, -80.64) * mm});
            skLineSegment(sketch, "E119.rect.top", {"start": v(254, -385.44) * mm, "end": v(-254, -385.44) * mm});
            skLineSegment(sketch, "E119.rect.left", {"start": v(279.4, -106.04) * mm, "end": v(279.4, -360.04) * mm});
            skLineSegment(sketch, "E119.rect.right", {"start": v(-279.4, -106.04) * mm, "end": v(-279.4, -360.04) * mm});
            skPoint(sketch, "E119.rect.middle", {"position": v(0, -233.04) * mm});
            skPoint(sketch, "E120.visualSharp", {"position": v(-279.4, -385.44) * mm});
            skArc(sketch, "E120.filletArc", {"start": v(-279.4, -360.04) * mm, "mid": v(-271.96, -378) * mm, "end": v(-254, -385.44) * mm});
            skPoint(sketch, "E121.visualSharp", {"position": v(279.4, -385.44) * mm});
            skArc(sketch, "E121.filletArc", {"start": v(254, -385.44) * mm, "mid": v(271.96, -378) * mm, "end": v(279.4, -360.04) * mm});
            skPoint(sketch, "E122.visualSharp", {"position": v(-279.4, -80.64) * mm});
            skArc(sketch, "E122.filletArc", {"start": v(-254, -80.64) * mm, "mid": v(-271.96, -88.08) * mm, "end": v(-279.4, -106.04) * mm});
            skPoint(sketch, "E123.visualSharp", {"position": v(279.4, -80.64) * mm});
            skArc(sketch, "E123.filletArc", {"start": v(279.4, -106.04) * mm, "mid": v(271.96, -88.08) * mm, "end": v(254, -80.64) * mm});
            skLineSegment(sketch, "E124", {"start": v(0, -80.64) * mm, "end": v(0, -157.45) * mm, "construction": true});
            skLineSegment(sketch, "E125", {"start": v(-76.2, -157.45) * mm, "end": v(0, -157.45) * mm, "construction": true});
            skLineSegment(sketch, "E126", {"start": v(0, -157.45) * mm, "end": v(0, -234.25) * mm, "construction": true});
            skLineSegment(sketch, "E127", {"start": v(0, -157.45) * mm, "end": v(76.2, -157.45) * mm, "construction": true});
            skLineSegment(sketch, "E128", {"start": v(0, -80.64) * mm, "end": v(0, -385.44) * mm, "construction": true});
            skSolve(sketch);
        }
        {
            var Q0;
            {var subQ1=sQuery(id+"F37.wireOp",EDGE,"E117");var subQ3=makeQuery(id+"F38.opExtrude","CAP_EDGE",EDGE,{"disambiguationData":[OSD([subQ1])],"isStart":true});Q0=makeQuery(id+"F39.imprint","IMPRINT",FACE,{"disambiguationData":[TD([[makeQuery(id+"F39.imprint","IMPRINT",EDGE,{"derivedFrom":subQ3}),1.0]])]});}
            var Q1;
            Q1=makeQuery(id+"F39.imprint","IMPRINT",FACE,{"disambiguationData":[TD([[makeQuery(id+"F39.imprint","IMPRINT",EDGE,{"derivedFrom":sQuery(id+"F39.wireOp",EDGE,"E119.rect.top")}),-1.0]])]});
            extrude(context, id + "F40", {"entities" : qUnion([Q0, Q1]), "depth" : 19.05 * mm});
        }
        {
            var Q0;
            Q0=makeQuery(id+"F34.opExtrude","SWEPT_FACE",FACE,{"disambiguationData":[OSD([sQuery(id+"F33.wireOp",EDGE,"E111")])]});
            var sketch = newSketch(context, id + "F41", { "sketchPlane" : qUnion([Q0])});
            skLineSegment(sketch, "E129", {"start": v(-472.41, -223.78) * mm, "end": v(-378.73, -344.65) * mm, "construction": true});
            skLineSegment(sketch, "E130", {"start": v(-365.34, -237.54) * mm, "end": v(-485.8, -330.9) * mm, "construction": true});
            skLineSegment(sketch, "E131.rect.bottom", {"start": v(-292.06, -373.55) * mm, "end": v(-693.57, -684.76) * mm});
            skLineSegment(sketch, "E131.rect.top", {"start": v(-478.78, -132.64) * mm, "end": v(-880.3, -443.85) * mm});
            skLineSegment(sketch, "E131.rect.left", {"start": v(-287.54, -337.91) * mm, "end": v(-443.15, -137.16) * mm});
            skLineSegment(sketch, "E131.rect.right", {"start": v(-729.2, -680.24) * mm, "end": v(-884.8, -479.49) * mm});
            skPoint(sketch, "E131.rect.middle", {"position": v(-586.18, -408.7) * mm});
            skPoint(sketch, "E132.visualSharp", {"position": v(-900.37, -459.41) * mm});
            skArc(sketch, "E132.filletArc", {"start": v(-880.3, -443.85) * mm, "mid": v(-889.93, -460.73) * mm, "end": v(-884.8, -479.49) * mm});
            skPoint(sketch, "E133.visualSharp", {"position": v(-458.7, -117.08) * mm});
            skArc(sketch, "E133.filletArc", {"start": v(-443.15, -137.16) * mm, "mid": v(-460.03, -127.52) * mm, "end": v(-478.78, -132.64) * mm});
            skPoint(sketch, "E134.visualSharp", {"position": v(-271.98, -357.99) * mm});
            skArc(sketch, "E134.filletArc", {"start": v(-292.06, -373.55) * mm, "mid": v(-282.42, -356.67) * mm, "end": v(-287.54, -337.91) * mm});
            skPoint(sketch, "E135.visualSharp", {"position": v(-713.64, -700.32) * mm});
            skArc(sketch, "E135.filletArc", {"start": v(-729.2, -680.24) * mm, "mid": v(-712.32, -689.88) * mm, "end": v(-693.57, -684.76) * mm});
            skLineSegment(sketch, "E136", {"start": v(-365.34, -237.54) * mm, "end": v(-807, -579.87) * mm, "construction": true});
            skSolve(sketch);
        }
        {
            var Q0;
            Q0=makeQuery(id+"F41.imprint","IMPRINT",FACE,{"disambiguationData":[TD([[makeQuery(id+"F41.imprint","IMPRINT",EDGE,{"derivedFrom":sQuery(id+"F41.wireOp",EDGE,"E131.rect.bottom")}),-1.0]])]});
            var Q1;
            {var subQ1=sQuery(id+"F33.wireOp",EDGE,"E111");Q1=makeQuery(id+"F41.imprint","IMPRINT",FACE,{"disambiguationData":[TD([[makeQuery(id+"F41.imprint","IMPRINT",EDGE,{"derivedFrom":makeQuery(id+"F34.opExtrude","CAP_EDGE",EDGE,{"disambiguationData":[OSD([subQ1])],"isStart":true})}),1.0]])]});}
            extrude(context, id + "F42", {"entities" : qUnion([Q0, Q1]), "depth" : 19.05 * mm});
        }
        {
            var Q0;
            Q0=makeQuery(id+"F32.opExtrude","SWEPT_FACE",FACE,{"disambiguationData":[OSD([sQuery(id+"F31.wireOp",EDGE,"E108")])]});
            var sketch = newSketch(context, id + "F43", { "sketchPlane" : qUnion([Q0])});
            skLineSegment(sketch, "E137", {"start": v(365.34, -237.54) * mm, "end": v(485.8, -330.9) * mm, "construction": true});
            skLineSegment(sketch, "E138", {"start": v(472.41, -223.78) * mm, "end": v(378.73, -344.65) * mm, "construction": true});
            skLineSegment(sketch, "E139.rect.bottom", {"start": v(693.57, -684.76) * mm, "end": v(292.06, -373.55) * mm});
            skLineSegment(sketch, "E139.rect.top", {"start": v(880.3, -443.85) * mm, "end": v(478.78, -132.64) * mm});
            skLineSegment(sketch, "E139.rect.left", {"start": v(729.2, -680.24) * mm, "end": v(884.8, -479.49) * mm});
            skLineSegment(sketch, "E139.rect.right", {"start": v(287.54, -337.91) * mm, "end": v(443.15, -137.16) * mm});
            skPoint(sketch, "E139.rect.middle", {"position": v(586.18, -408.7) * mm});
            skPoint(sketch, "E140.visualSharp", {"position": v(458.7, -117.08) * mm});
            skArc(sketch, "E140.filletArc", {"start": v(478.78, -132.64) * mm, "mid": v(460.03, -127.52) * mm, "end": v(443.15, -137.16) * mm});
            skPoint(sketch, "E141.visualSharp", {"position": v(900.37, -459.41) * mm});
            skArc(sketch, "E141.filletArc", {"start": v(884.8, -479.49) * mm, "mid": v(889.93, -460.73) * mm, "end": v(880.3, -443.85) * mm});
            skPoint(sketch, "E142.visualSharp", {"position": v(713.64, -700.32) * mm});
            skArc(sketch, "E142.filletArc", {"start": v(693.57, -684.76) * mm, "mid": v(712.32, -689.88) * mm, "end": v(729.2, -680.24) * mm});
            skPoint(sketch, "E143.visualSharp", {"position": v(271.98, -357.99) * mm});
            skArc(sketch, "E143.filletArc", {"start": v(287.54, -337.91) * mm, "mid": v(282.42, -356.67) * mm, "end": v(292.06, -373.55) * mm});
            skLineSegment(sketch, "E144", {"start": v(365.34, -237.54) * mm, "end": v(807, -579.87) * mm, "construction": true});
            skSolve(sketch);
        }
        {
            var Q0;
            Q0=makeQuery(id+"F43.imprint","IMPRINT",FACE,{"disambiguationData":[TD([[makeQuery(id+"F43.imprint","IMPRINT",EDGE,{"derivedFrom":sQuery(id+"F43.wireOp",EDGE,"E139.rect.bottom")}),-1.0]])]});
            var Q1;
            {var subQ1=sQuery(id+"F31.wireOp",EDGE,"E108");Q1=makeQuery(id+"F43.imprint","IMPRINT",FACE,{"disambiguationData":[TD([[makeQuery(id+"F43.imprint","IMPRINT",EDGE,{"derivedFrom":makeQuery(id+"F32.opExtrude","CAP_EDGE",EDGE,{"disambiguationData":[OSD([subQ1])],"isStart":true})}),-1.0]])]});}
            extrude(context, id + "F44", {"entities" : qUnion([Q0, Q1]), "depth" : 19.05 * mm});
        }
    });
